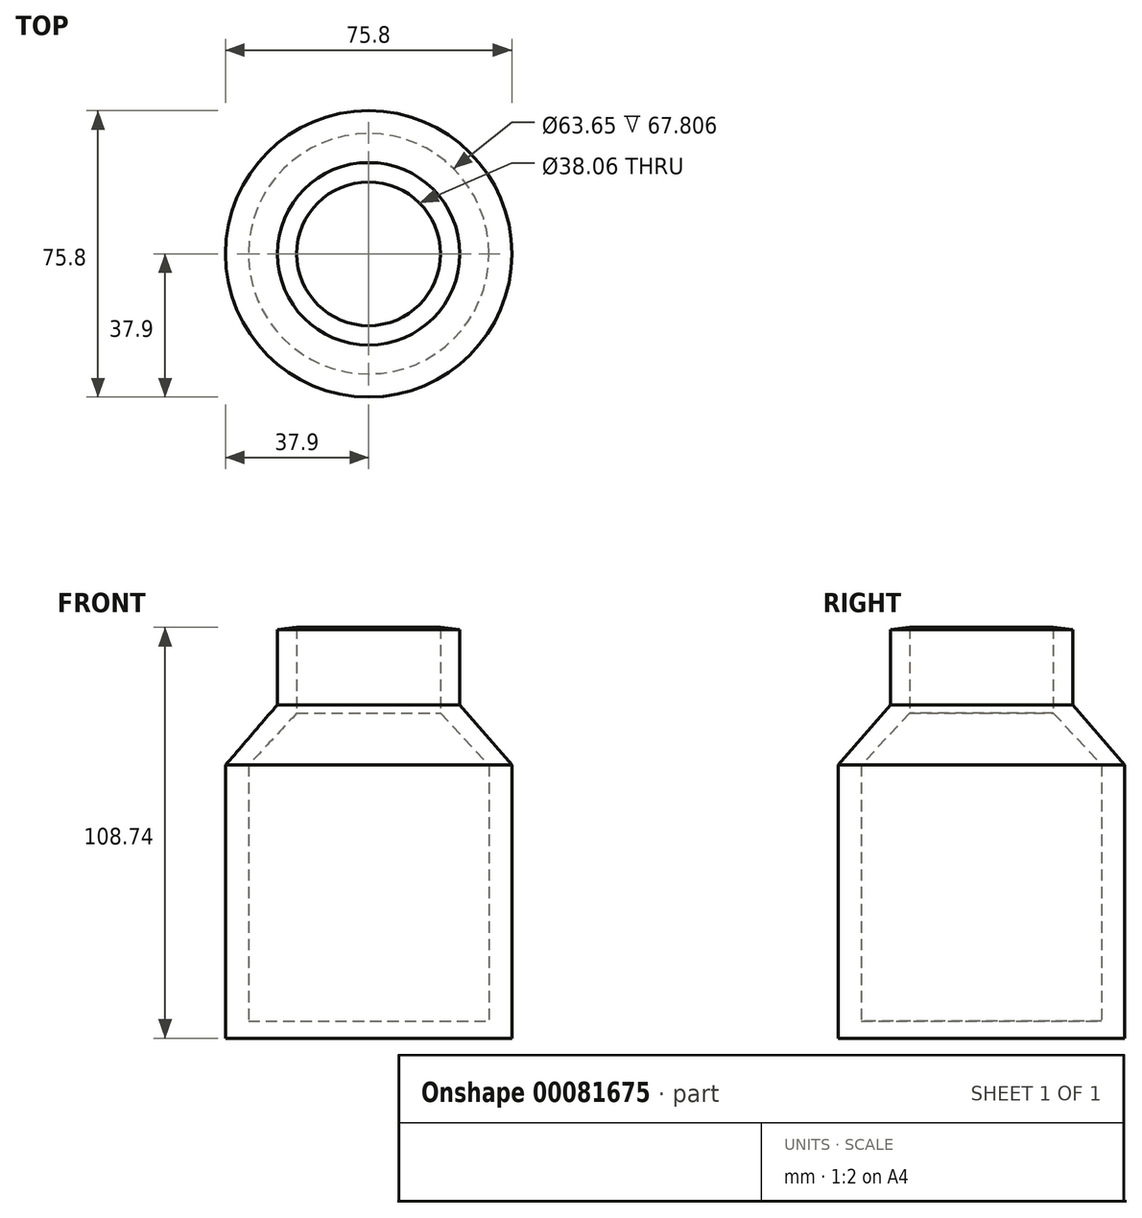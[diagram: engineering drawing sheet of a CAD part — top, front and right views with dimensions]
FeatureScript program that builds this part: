
annotation { "Feature Type Name" : "Feature", "Feature Type Description" : "" }
export const myFeature = defineFeature(function(context is Context, id is Id, definition is map)
    precondition{}
    {
        {
            var Q0;
            Q0=qCreatedBy(makeId("Front.planeOp"),FACE);
            var sketch = newSketch(context, id + "F0", { "sketchPlane" : qUnion([Q0])});
            skLineSegment(sketch, "E0", {"start": v(-24.15, 52.93) * mm, "end": v(-24.15, 33.1) * mm});
            skLineSegment(sketch, "E1", {"start": v(-24.15, 33.1) * mm, "end": v(-37.9, 17.1) * mm});
            skLineSegment(sketch, "E2", {"start": v(-37.9, 17.1) * mm, "end": v(-37.9, -55.17) * mm});
            skLineSegment(sketch, "E3", {"start": v(-37.9, -55.17) * mm, "end": v(0, -55.17) * mm});
            skLineSegment(sketch, "E4", {"start": v(0, -55.17) * mm, "end": v(0, -50.7) * mm});
            skLineSegment(sketch, "E5", {"start": v(0, -50.7) * mm, "end": v(-31.82, -50.7) * mm});
            skLineSegment(sketch, "E6", {"start": v(-31.82, -50.7) * mm, "end": v(-31.82, 17.1) * mm});
            skLineSegment(sketch, "E7", {"start": v(-31.82, 17.1) * mm, "end": v(-19.03, 30.86) * mm});
            skLineSegment(sketch, "E8", {"start": v(-19.03, 30.86) * mm, "end": v(-19.03, 53.57) * mm});
            skLineSegment(sketch, "E9", {"start": v(-19.03, 53.57) * mm, "end": v(-24.15, 52.93) * mm});
            skSolve(sketch);
        }
        {
            var Q0;
            Q0=makeQuery(id+"F0.imprint","IMPRINT",FACE,{"disambiguationData":[TD([[makeQuery(id+"F0.imprint","IMPRINT",EDGE,{"derivedFrom":sQuery(id+"F0.wireOp",EDGE,"E0")}),1.0]])]});
            var Q1;
            Q1=sQuery(id+"F0.wireOp",EDGE,"E4");
            revolve(context, id + "F1", {"entities" : qUnion([Q0]), "axis" : qUnion([Q1]), "revolveType" : RevolveType.FULL});
        }
    });
